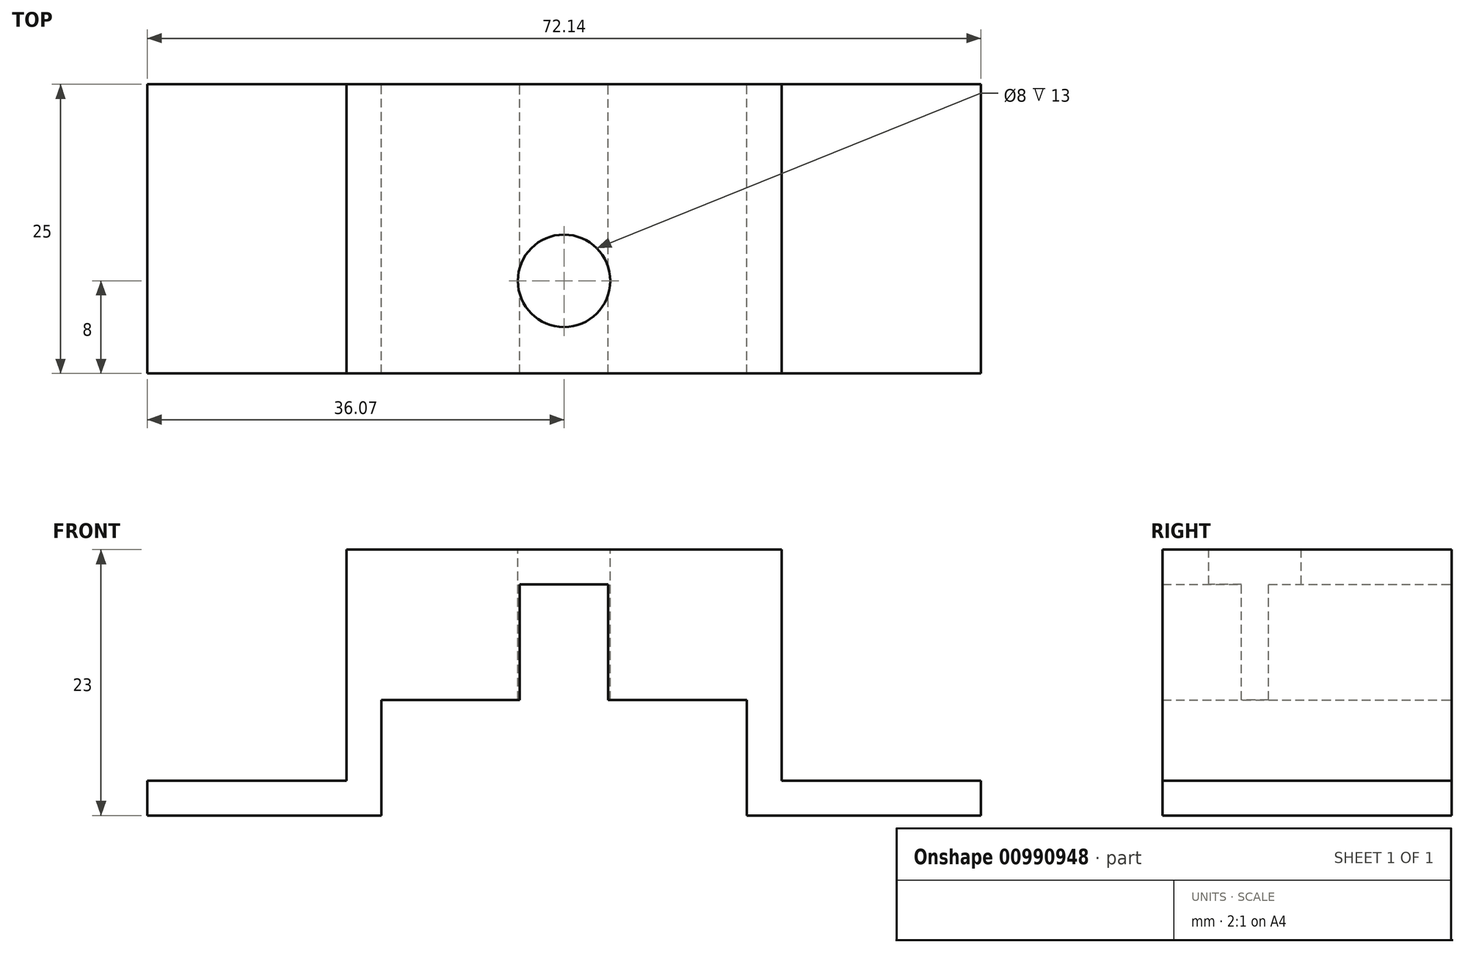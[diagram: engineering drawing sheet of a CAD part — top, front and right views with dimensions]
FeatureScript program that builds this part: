
annotation { "Feature Type Name" : "Feature", "Feature Type Description" : "" }
export const myFeature = defineFeature(function(context is Context, id is Id, definition is map)
    precondition{}
    {
        {
            var Q0;
            Q0=qCreatedBy(makeId("Front.planeOp"),FACE);
            var sketch = newSketch(context, id + "F0", { "sketchPlane" : qUnion([Q0])});
            skLineSegment(sketch, "E0.top", {"start": v(15.82, 10) * mm, "end": v(-15.82, 10) * mm});
            skLineSegment(sketch, "E0.left", {"start": v(15.82, -10) * mm, "end": v(15.82, 10) * mm});
            skLineSegment(sketch, "E0.right", {"start": v(-15.82, -10) * mm, "end": v(-15.82, 10) * mm});
            skPoint(sketch, "E0.middle", {"position": v(0, 0) * mm});
            skLineSegment(sketch, "E1", {"start": v(-15.82, -10) * mm, "end": v(-36.07, -10) * mm});
            skLineSegment(sketch, "E2", {"start": v(-36.07, -10) * mm, "end": v(-36.07, -7) * mm});
            skLineSegment(sketch, "E3", {"start": v(-36.07, -7) * mm, "end": v(-18.82, -7) * mm});
            skLineSegment(sketch, "E4", {"start": v(-18.82, -7) * mm, "end": v(-18.82, 13) * mm});
            skLineSegment(sketch, "E5", {"start": v(-18.82, 13) * mm, "end": v(0, 13) * mm});
            skLineSegment(sketch, "E6", {"start": v(0, 13) * mm, "end": v(0, -13.4) * mm, "construction": true});
            skPoint(sketch, "E6.endSnap0", {"position": v(0, -7.4) * mm});
            skLineSegment(sketch, "E7.MirrorCS", {"start": v(18.82, 13) * mm, "end": v(0, 13) * mm});
            skLineSegment(sketch, "E8.MirrorCS", {"start": v(18.82, -7) * mm, "end": v(18.82, 13) * mm});
            skLineSegment(sketch, "E9.MirrorCS", {"start": v(36.07, -7) * mm, "end": v(18.82, -7) * mm});
            skLineSegment(sketch, "E10.MirrorCS", {"start": v(15.82, -10) * mm, "end": v(36.07, -10) * mm});
            skLineSegment(sketch, "E11.MirrorCS", {"start": v(36.07, -10) * mm, "end": v(36.07, -7) * mm});
            skLineSegment(sketch, "E12.top", {"start": v(-15.82, 0) * mm, "end": v(-3.82, 0) * mm});
            skLineSegment(sketch, "E12.right", {"start": v(-3.82, 10) * mm, "end": v(-3.82, 0) * mm});
            skLineSegment(sketch, "E13.MirrorCS", {"start": v(3.82, 10) * mm, "end": v(3.82, 0) * mm});
            skLineSegment(sketch, "E14.MirrorCS", {"start": v(15.82, 0) * mm, "end": v(3.82, 0) * mm});
            skSolve(sketch);
        }
        {
            var Q0;
            Q0=makeQuery(id+"F0.imprint","IMPRINT",FACE,{"disambiguationData":[TD([[makeQuery(id+"F0.imprint","IMPRINT",EDGE,{"derivedFrom":sQuery(id+"F0.wireOp",EDGE,"E0.top")}),-1.0]])]});
            var Q1;
            {var subQ4=sQuery(id+"F0.wireOp",EDGE,"E12.top");Q1=makeQuery(id+"F0.imprint","IMPRINT",FACE,{"disambiguationData":[TD([[makeQuery(id+"F0.imprint","IMPRINT",EDGE,{"derivedFrom":subQ4}),1.0]])]});}
            var Q2;
            {var subQ3=sQuery(id+"F0.wireOp",EDGE,"E13.MirrorCS");Q2=makeQuery(id+"F0.imprint","IMPRINT",FACE,{"disambiguationData":[TD([[makeQuery(id+"F0.imprint","IMPRINT",EDGE,{"derivedFrom":subQ3}),1.0]])]});}
            extrude(context, id + "F1", {"entities" : qUnion([Q0, Q1, Q2]), "depth" : 25 * mm, "offsetDistance" : 25 * mm});
        }
        {
            var Q0;
            Q0=makeQuery(id+"F1.opExtrude","SWEPT_FACE",FACE,{"disambiguationData":[OSD([sQuery(id+"F0.wireOp",EDGE,"E5"),sQuery(id+"F0.wireOp",EDGE,"E7.MirrorCS")])]});
            var sketch = newSketch(context, id + "F2", { "sketchPlane" : qUnion([Q0])});
            skCircle(sketch, "E15", {"center": v(0, -17) * mm, "radius": 4 * mm});
            skSolve(sketch);
        }
        {
            var Q0;
            Q0=makeQuery(id+"F2.imprint","IMPRINT",FACE,{"disambiguationData":[TD([[makeQuery(id+"F2.imprint","IMPRINT",EDGE,{"derivedFrom":sQuery(id+"F2.wireOp",EDGE,"E15")}),1.0]])]});
            extrude(context, id + "F3", {"entities" : qUnion([Q0]), "operationType" : NewBodyOperationType.REMOVE, "endBound" : BoundingType.THROUGH_ALL, "oppositeDirection" : true, "depth" : 25 * mm, "offsetDistance" : 25 * mm});
        }
    });
